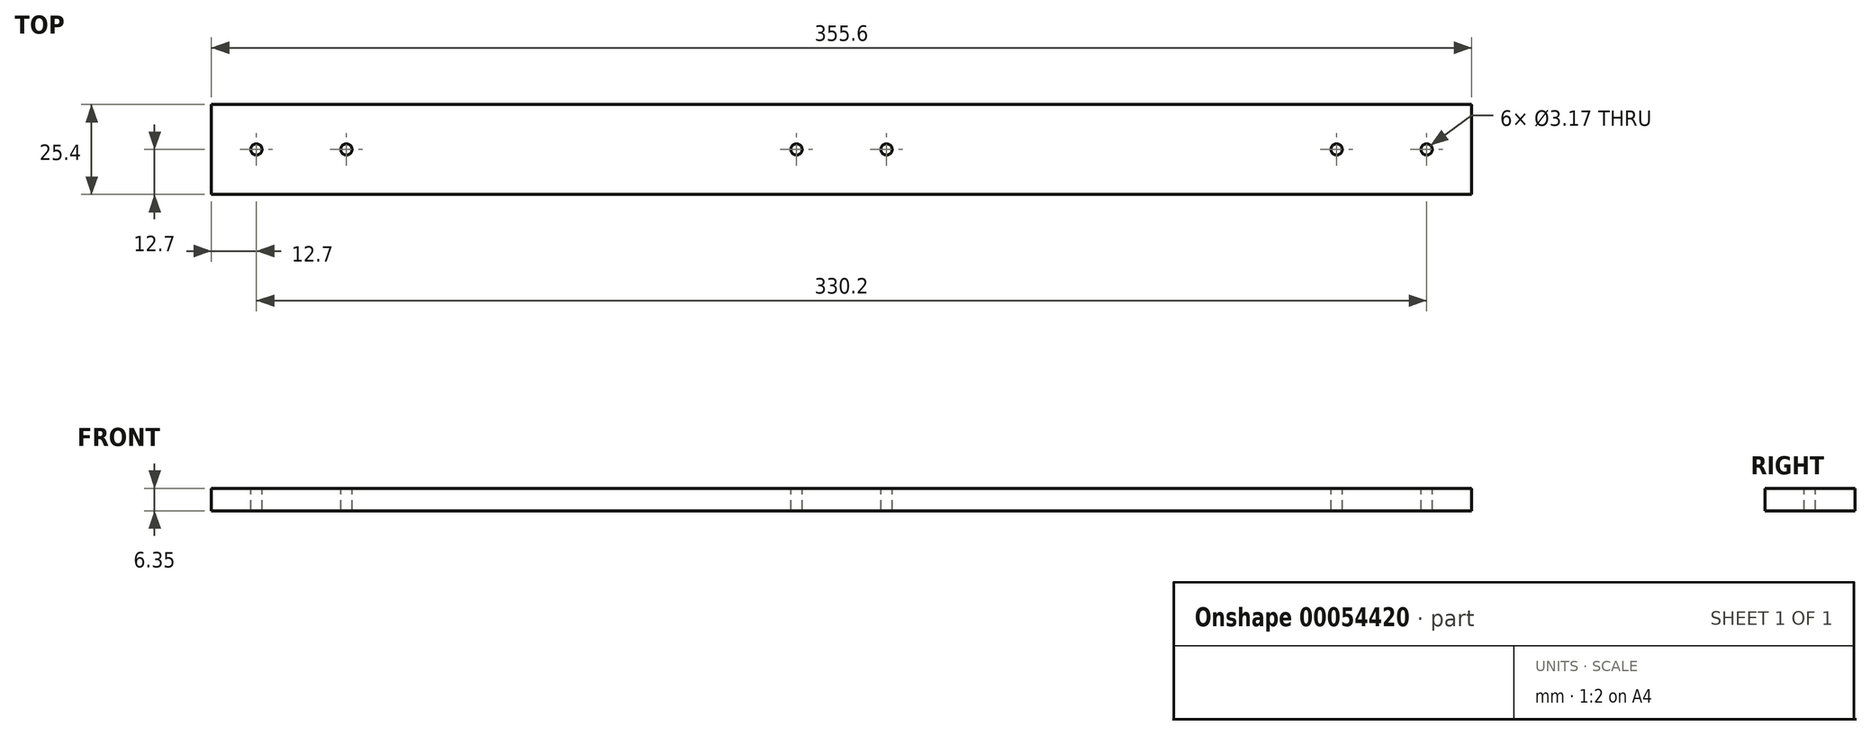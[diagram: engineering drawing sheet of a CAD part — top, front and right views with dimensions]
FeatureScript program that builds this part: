
annotation { "Feature Type Name" : "Feature", "Feature Type Description" : "" }
export const myFeature = defineFeature(function(context is Context, id is Id, definition is map)
    precondition{}
    {
        {
            var Q0;
            Q0=qCreatedBy(makeId("Top.planeOp"),FACE);
            var sketch = newSketch(context, id + "F0", { "sketchPlane" : qUnion([Q0])});
            skLineSegment(sketch, "E0.bottom", {"start": v(0, 0) * mm, "end": v(355.6, 0) * mm});
            skLineSegment(sketch, "E0.top", {"start": v(0, 25.4) * mm, "end": v(355.6, 25.4) * mm});
            skLineSegment(sketch, "E0.left", {"start": v(0, 0) * mm, "end": v(0, 25.4) * mm});
            skLineSegment(sketch, "E0.right", {"start": v(355.6, 0) * mm, "end": v(355.6, 25.4) * mm});
            skSolve(sketch);
        }
        {
            var Q0;
            Q0=makeQuery(id+"F0.imprint","IMPRINT",FACE,{"disambiguationData":[TD([[makeQuery(id+"F0.imprint","IMPRINT",EDGE,{"derivedFrom":sQuery(id+"F0.wireOp",EDGE,"E0.bottom")}),1.0]])]});
            extrude(context, id + "F1", {"entities" : qUnion([Q0]), "depth" : 6.35 * mm});
        }
        {
            var Q0;
            Q0=makeQuery(id+"F1.opExtrude","CAP_FACE",FACE,{"disambiguationData":[OSD([sQuery(id+"F0.wireOp",EDGE,"E0.bottom"),sQuery(id+"F0.wireOp",EDGE,"E0.top"),sQuery(id+"F0.wireOp",EDGE,"E0.left"),sQuery(id+"F0.wireOp",EDGE,"E0.right")])],"isStart":false});
            var sketch = newSketch(context, id + "F2", { "sketchPlane" : qUnion([Q0])});
            skLineSegment(sketch, "E1", {"start": v(177.8, 25.4) * mm, "end": v(177.8, 0) * mm});
            skPoint(sketch, "E2", {"position": v(165.1, 12.7) * mm});
            skPoint(sketch, "E3.MirrorP", {"position": v(190.5, 12.7) * mm});
            skSolve(sketch);
        }
        {
            var Q0;
            Q0=sQuery(id+"F2.wireOp",VERTEX,"E2");
            var Q1;
            Q1=sQuery(id+"F2.wireOp",VERTEX,"E3.MirrorP");
            var Q2;
            Q2=makeQuery(id+"F1.opExtrude","SWEPT_BODY",BODY,{"disambiguationData":[OSD([sQuery(id+"F0.wireOp",EDGE,"E0.bottom"),sQuery(id+"F0.wireOp",EDGE,"E0.top"),sQuery(id+"F0.wireOp",EDGE,"E0.left"),sQuery(id+"F0.wireOp",EDGE,"E0.right")])]});
            hole(context, id + "F3", {"style" : HoleStyle.SIMPLE, "holeDiameter" : 3.17 * mm, "endStyle" : HoleEndStyle.THROUGH, "locations" : qUnion([Q0, Q1]), "scope" : qUnion([Q2])});
        }
        {
            var Q0;
            Q0=makeQuery(id+"F1.opExtrude","CAP_FACE",FACE,{"disambiguationData":[OSD([sQuery(id+"F0.wireOp",EDGE,"E0.bottom"),sQuery(id+"F0.wireOp",EDGE,"E0.top"),sQuery(id+"F0.wireOp",EDGE,"E0.left"),sQuery(id+"F0.wireOp",EDGE,"E0.right")])],"isStart":false});
            var sketch = newSketch(context, id + "F4", { "sketchPlane" : qUnion([Q0])});
            skLineSegment(sketch, "E4", {"start": v(0, 12.7) * mm, "end": v(355.6, 12.7) * mm});
            skLineSegment(sketch, "E5", {"start": v(177.8, 25.4) * mm, "end": v(177.8, 0) * mm});
            skPoint(sketch, "E6", {"position": v(12.7, 12.7) * mm});
            skPoint(sketch, "E7.MirrorP", {"position": v(342.9, 12.7) * mm});
            skPoint(sketch, "E8", {"position": v(38.1, 12.7) * mm});
            skPoint(sketch, "E9.MirrorP", {"position": v(317.5, 12.7) * mm});
            skSolve(sketch);
        }
        {
            var Q0;
            Q0=sQuery(id+"F4.wireOp",VERTEX,"E6");
            var Q1;
            Q1=sQuery(id+"F4.wireOp",VERTEX,"E7.MirrorP");
            var Q2;
            Q2=sQuery(id+"F4.wireOp",VERTEX,"E8");
            var Q3;
            Q3=sQuery(id+"F4.wireOp",VERTEX,"E9.MirrorP");
            var Q4;
            Q4=makeQuery(id+"F1.opExtrude","SWEPT_BODY",BODY,{"disambiguationData":[OSD([sQuery(id+"F0.wireOp",EDGE,"E0.bottom"),sQuery(id+"F0.wireOp",EDGE,"E0.top"),sQuery(id+"F0.wireOp",EDGE,"E0.left"),sQuery(id+"F0.wireOp",EDGE,"E0.right")])]});
            hole(context, id + "F5", {"style" : HoleStyle.SIMPLE, "holeDiameter" : 3.17 * mm, "endStyle" : HoleEndStyle.THROUGH, "locations" : qUnion([Q0, Q1, Q2, Q3]), "scope" : qUnion([Q4])});
        }
    });
